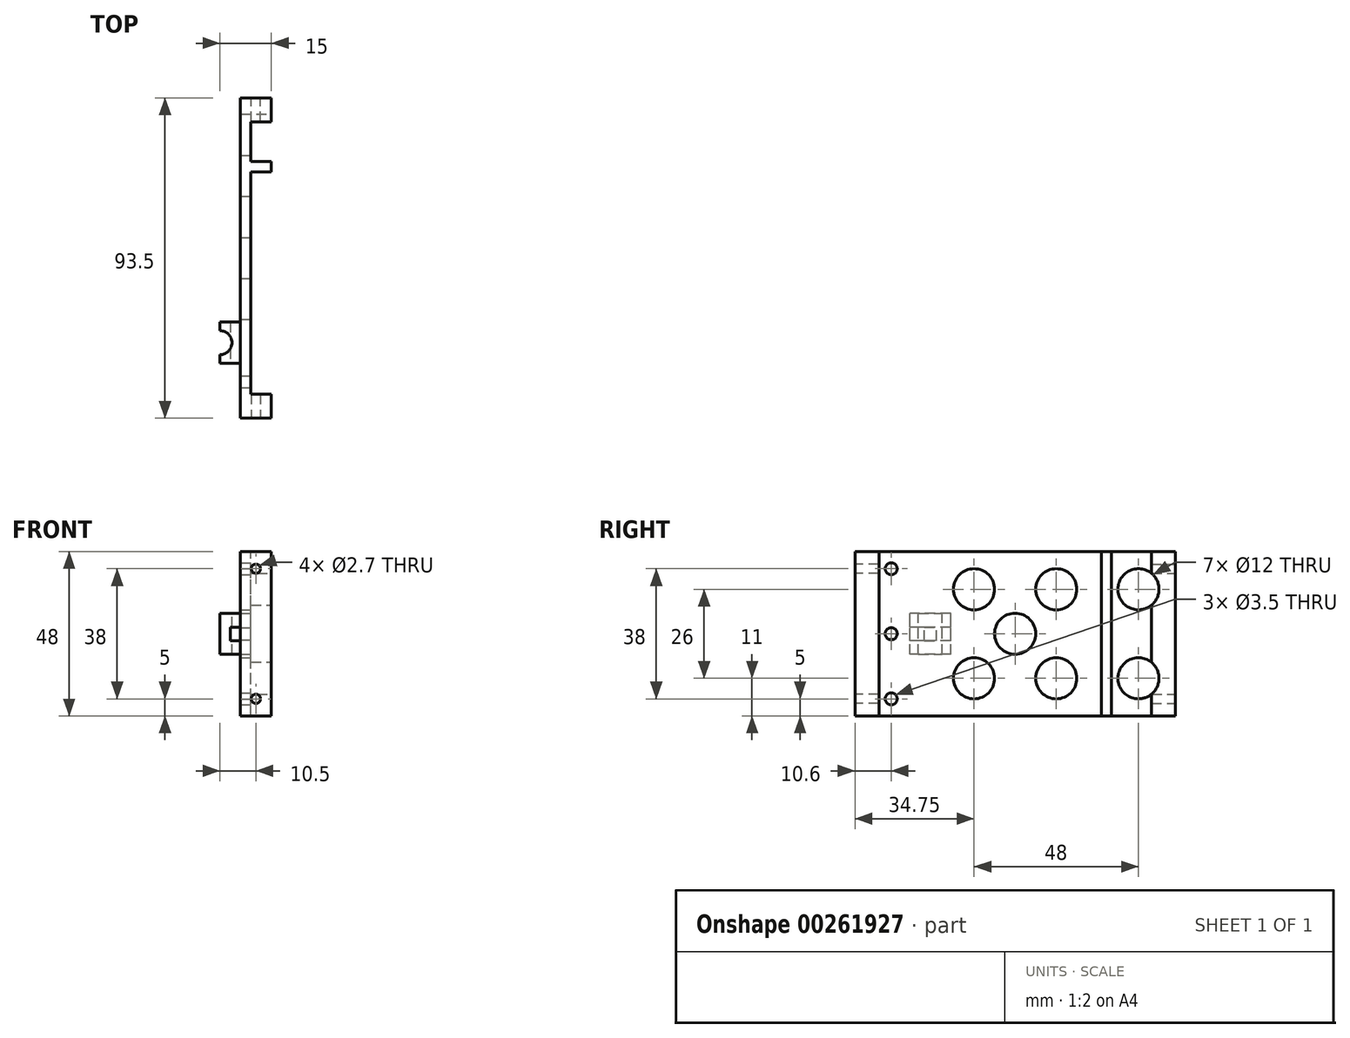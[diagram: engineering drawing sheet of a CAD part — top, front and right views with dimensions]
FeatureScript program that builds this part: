
annotation { "Feature Type Name" : "Feature", "Feature Type Description" : "" }
export const myFeature = defineFeature(function(context is Context, id is Id, definition is map)
    precondition{}
    {
        {
            var Q0;
            Q0=qCreatedBy(makeId("Top.planeOp"),FACE);
            var sketch = newSketch(context, id + "F0", { "sketchPlane" : qUnion([Q0])});
            skLineSegment(sketch, "E0.bottom", {"start": v(-4.5, 46.75) * mm, "end": v(4.5, 46.75) * mm});
            skLineSegment(sketch, "E0.top", {"start": v(-4.5, -46.75) * mm, "end": v(4.5, -46.75) * mm});
            skLineSegment(sketch, "E0.left", {"start": v(-4.5, 46.75) * mm, "end": v(-4.5, -46.75) * mm});
            skLineSegment(sketch, "E0.right", {"start": v(4.5, 46.75) * mm, "end": v(4.5, -46.75) * mm});
            skSolve(sketch);
        }
        {
            var Q0;
            Q0=qSketchRegion(id+"F0",true);
            extrude(context, id + "F1", {"entities" : qUnion([Q0]), "depth" : 48 * mm});
        }
        {
            var Q0;
            Q0=makeQuery(id+"F1.opExtrude","SWEPT_FACE",FACE,{"disambiguationData":[OSD([sQuery(id+"F0.wireOp",EDGE,"E0.top")])]});
            var sketch = newSketch(context, id + "F2", { "sketchPlane" : qUnion([Q0])});
            skCircle(sketch, "E1", {"center": v(0, 43) * mm, "radius": 1.35 * mm});
            skCircle(sketch, "E2", {"center": v(0, 5) * mm, "radius": 1.35 * mm});
            skLineSegment(sketch, "E3", {"start": v(-9.7, 24) * mm, "end": v(13.72, 24) * mm, "construction": true});
            skPoint(sketch, "E3.startSnap0", {"position": v(-4.5, 24) * mm});
            skSolve(sketch);
        }
        {
            var Q0;
            Q0=qSketchRegion(id+"F2",true);
            extrude(context, id + "F3", {"entities" : qUnion([Q0]), "operationType" : NewBodyOperationType.REMOVE, "oppositeDirection" : true, "depth" : 8 * mm});
        }
        {
            var Q0;
            Q0=makeQuery(id+"F1.opExtrude","SWEPT_FACE",FACE,{"disambiguationData":[OSD([sQuery(id+"F0.wireOp",EDGE,"E0.bottom")])]});
            var sketch = newSketch(context, id + "F4", { "sketchPlane" : qUnion([Q0])});
            skLineSegment(sketch, "E4", {"start": v(-8.54, 24) * mm, "end": v(11.95, 24) * mm, "construction": true});
            skPoint(sketch, "E4.startSnap0", {"position": v(-4.5, 24) * mm});
            skPoint(sketch, "E4.endSnap0", {"position": v(4.5, 24) * mm});
            skCircle(sketch, "E5", {"center": v(0, 43) * mm, "radius": 1.35 * mm});
            skCircle(sketch, "E6", {"center": v(0, 5) * mm, "radius": 1.35 * mm});
            skSolve(sketch);
        }
        {
            var Q0;
            Q0=qSketchRegion(id+"F4",true);
            extrude(context, id + "F5", {"entities" : qUnion([Q0]), "operationType" : NewBodyOperationType.REMOVE, "oppositeDirection" : true, "depth" : 8 * mm});
        }
        {
            var Q0;
            Q0=makeQuery(id+"F1.opExtrude","SWEPT_FACE",FACE,{"disambiguationData":[OSD([sQuery(id+"F0.wireOp",EDGE,"E0.right")])]});
            var sketch = newSketch(context, id + "F6", { "sketchPlane" : qUnion([Q0])});
            skLineSegment(sketch, "E7", {"start": v(-36.15, 53.21) * mm, "end": v(-36.15, -1.68) * mm, "construction": true});
            skLineSegment(sketch, "E8", {"start": v(-54.16, 24) * mm, "end": v(59.28, 24) * mm, "construction": true});
            skPoint(sketch, "E8.startSnap0", {"position": v(-46.75, 24) * mm});
            skCircle(sketch, "E9", {"center": v(-36.15, 43) * mm, "radius": 1.75 * mm});
            skCircle(sketch, "E10", {"center": v(-36.15, 24) * mm, "radius": 1.75 * mm});
            skCircle(sketch, "E11", {"center": v(-36.15, 5) * mm, "radius": 1.75 * mm});
            skSolve(sketch);
        }
        {
            var Q0;
            Q0=qSketchRegion(id+"F6",true);
            extrude(context, id + "F7", {"entities" : qUnion([Q0]), "operationType" : NewBodyOperationType.REMOVE, "endBound" : BoundingType.THROUGH_ALL, "oppositeDirection" : true, "depth" : 25 * mm});
        }
        {
            var Q0;
            Q0=makeQuery(id+"F1.opExtrude","SWEPT_FACE",FACE,{"disambiguationData":[OSD([sQuery(id+"F0.wireOp",EDGE,"E0.right")])]});
            var sketch = newSketch(context, id + "F8", { "sketchPlane" : qUnion([Q0])});
            skCircle(sketch, "E12", {"center": v(-12, 11) * mm, "radius": 6 * mm});
            skLineSegment(sketch, "E13", {"start": v(-49.95, 24) * mm, "end": v(48.97, 24) * mm, "construction": true});
            skPoint(sketch, "E13.startSnap0", {"position": v(-46.75, 24) * mm});
            skLineSegment(sketch, "E14", {"start": v(-12, -17.35) * mm, "end": v(-12, 65.96) * mm, "construction": true});
            skLineSegment(sketch, "E15", {"start": v(12, -17.71) * mm, "end": v(12, 67.42) * mm, "construction": true});
            skCircle(sketch, "E16", {"center": v(0, 24) * mm, "radius": 6 * mm});
            skLineSegment(sketch, "E17", {"start": v(24, -17.96) * mm, "end": v(24, 67.9) * mm, "construction": true});
            skLineSegment(sketch, "E18", {"start": v(36, -24.91) * mm, "end": v(36, 66.45) * mm, "construction": true});
            skLineSegment(sketch, "E19", {"start": v(-49.95, 11) * mm, "end": v(49.95, 11) * mm, "construction": true});
            skLineSegment(sketch, "E20", {"start": v(-49.95, 37) * mm, "end": v(50.2, 37) * mm, "construction": true});
            skCircle(sketch, "E21", {"center": v(-12, 37) * mm, "radius": 6 * mm});
            skCircle(sketch, "E22", {"center": v(12, 11) * mm, "radius": 6 * mm});
            skCircle(sketch, "E23", {"center": v(12, 37) * mm, "radius": 6 * mm});
            skCircle(sketch, "E24", {"center": v(36, 11) * mm, "radius": 6 * mm});
            skCircle(sketch, "E25", {"center": v(36, 37) * mm, "radius": 6 * mm});
            skSolve(sketch);
        }
        {
            var Q0;
            Q0=qSketchRegion(id+"F8",true);
            extrude(context, id + "F9", {"entities" : qUnion([Q0]), "operationType" : NewBodyOperationType.REMOVE, "endBound" : BoundingType.THROUGH_ALL, "oppositeDirection" : true, "depth" : 25 * mm});
        }
        {
            var Q0;
            Q0=makeQuery(id+"F1.opExtrude","CAP_FACE",FACE,{"disambiguationData":[OSD([sQuery(id+"F0.wireOp",EDGE,"E0.bottom"),sQuery(id+"F0.wireOp",EDGE,"E0.top"),sQuery(id+"F0.wireOp",EDGE,"E0.left"),sQuery(id+"F0.wireOp",EDGE,"E0.right")])],"isStart":false});
            var sketch = newSketch(context, id + "F10", { "sketchPlane" : qUnion([Q0])});
            skLineSegment(sketch, "E26.bottom", {"start": v(-1.5, -39.75) * mm, "end": v(4.5, -39.75) * mm});
            skLineSegment(sketch, "E26.top", {"start": v(-1.5, 25.15) * mm, "end": v(4.5, 25.15) * mm});
            skLineSegment(sketch, "E26.left", {"start": v(-1.5, -39.75) * mm, "end": v(-1.5, 25.15) * mm});
            skLineSegment(sketch, "E26.right", {"start": v(4.5, -39.75) * mm, "end": v(4.5, 25.15) * mm});
            skLineSegment(sketch, "E27.bottom", {"start": v(4.5, 28.15) * mm, "end": v(-1.5, 28.15) * mm});
            skLineSegment(sketch, "E27.top", {"start": v(4.5, 39.75) * mm, "end": v(-1.5, 39.75) * mm});
            skLineSegment(sketch, "E27.left", {"start": v(4.5, 28.15) * mm, "end": v(4.5, 39.75) * mm});
            skLineSegment(sketch, "E27.right", {"start": v(-1.5, 28.15) * mm, "end": v(-1.5, 39.75) * mm});
            skSolve(sketch);
        }
        {
            var Q0;
            Q0=qSketchRegion(id+"F10",true);
            extrude(context, id + "F11", {"entities" : qUnion([Q0]), "operationType" : NewBodyOperationType.REMOVE, "endBound" : BoundingType.THROUGH_ALL, "oppositeDirection" : true, "depth" : 25 * mm});
        }
        {
            var Q0;
            Q0=makeQuery(id+"F1.opExtrude","SWEPT_FACE",FACE,{"disambiguationData":[OSD([sQuery(id+"F0.wireOp",EDGE,"E0.left")])]});
            var sketch = newSketch(context, id + "F12", { "sketchPlane" : qUnion([Q0])});
            skLineSegment(sketch, "E28.bottom", {"start": v(18.75, 18) * mm, "end": v(30.75, 18) * mm});
            skLineSegment(sketch, "E28.top", {"start": v(18.75, 30) * mm, "end": v(30.75, 30) * mm});
            skLineSegment(sketch, "E28.left", {"start": v(18.75, 18) * mm, "end": v(18.75, 30) * mm});
            skLineSegment(sketch, "E28.right", {"start": v(30.75, 18) * mm, "end": v(30.75, 30) * mm});
            skLineSegment(sketch, "E29", {"start": v(46.75, 24) * mm, "end": v(14.26, 24) * mm, "construction": true});
            skSolve(sketch);
        }
        {
            var Q0;
            Q0 = qSketchRegion(id + "F12", true);
            extrude(context, id + "F13", {"entities" : qUnion([Q0]), "operationType" : NewBodyOperationType.ADD, "depth" : 6 * mm});
        }
        {
            var Q0;
            Q0=makeQuery(id+"F13.opExtrude","SWEPT_FACE",FACE,{"disambiguationData":[OSD([sQuery(id+"F12.wireOp",EDGE,"E28.right")])]});
            var sketch = newSketch(context, id + "F14", { "sketchPlane" : qUnion([Q0])});
            skLineSegment(sketch, "E30.bottom", {"start": v(-4.5, 21.96) * mm, "end": v(-7.5, 21.96) * mm});
            skLineSegment(sketch, "E30.top", {"start": v(-4.5, 25.96) * mm, "end": v(-7.5, 25.96) * mm});
            skLineSegment(sketch, "E30.left", {"start": v(-4.5, 21.96) * mm, "end": v(-4.5, 25.96) * mm});
            skLineSegment(sketch, "E30.right", {"start": v(-7.5, 21.96) * mm, "end": v(-7.5, 25.96) * mm});
            skSolve(sketch);
        }
        {
            var Q0;
            Q0 = qSketchRegion(id + "F14", true);
            extrude(context, id + "F15", {"entities" : qUnion([Q0]), "operationType" : NewBodyOperationType.REMOVE, "endBound" : BoundingType.UP_TO_NEXT, "oppositeDirection" : true, "depth" : 25 * mm});
        }
        {
            var Q0;
            Q0=makeQuery(id+"F13.opExtrude","SWEPT_FACE",FACE,{"disambiguationData":[OSD([sQuery(id+"F12.wireOp",EDGE,"E28.top")])]});
            var sketch = newSketch(context, id + "F16", { "sketchPlane" : qUnion([Q0])});
            skCircle(sketch, "E31", {"center": v(-10.5, -24.75) * mm, "radius": 3.5 * mm});
            skSolve(sketch);
        }
        {
            var Q0;
            Q0 = qSketchRegion(id + "F16", true);
            extrude(context, id + "F17", {"entities" : qUnion([Q0]), "operationType" : NewBodyOperationType.REMOVE, "endBound" : BoundingType.THROUGH_ALL, "oppositeDirection" : true, "depth" : 25 * mm});
        }
    });
